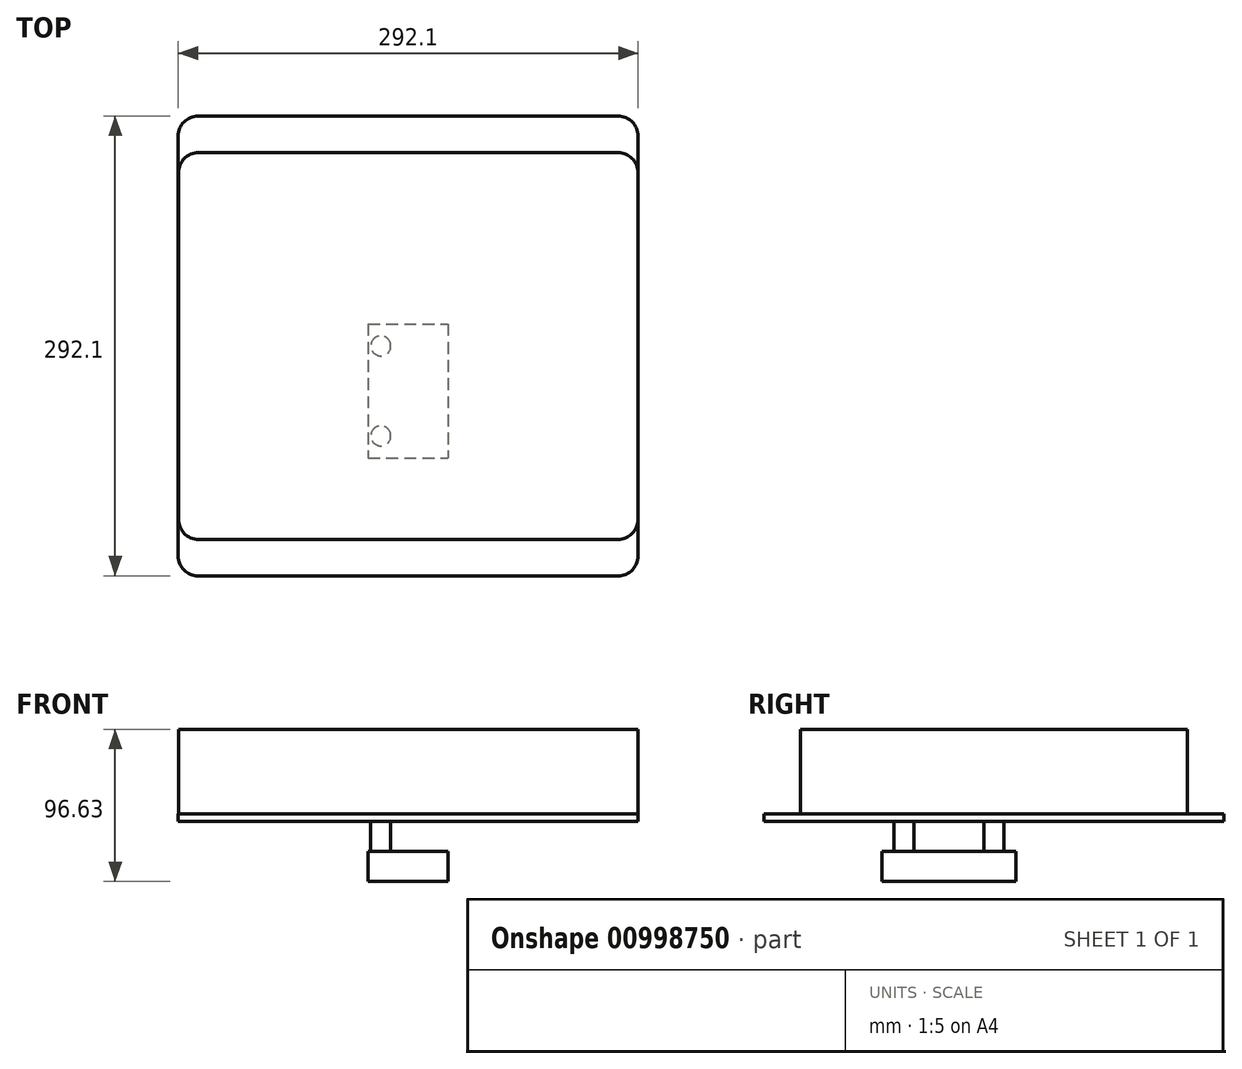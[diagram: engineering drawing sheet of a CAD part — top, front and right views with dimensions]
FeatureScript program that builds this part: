
annotation { "Feature Type Name" : "Feature", "Feature Type Description" : "" }
export const myFeature = defineFeature(function(context is Context, id is Id, definition is map)
    precondition{}
    {
        {
            var Q0;
            Q0=qCreatedBy(makeId("Top.planeOp"),FACE);
            var sketch = newSketch(context, id + "F0", { "sketchPlane" : qUnion([Q0])});
            skLineSegment(sketch, "E0.bottom", {"start": v(133.35, 146.05) * mm, "end": v(-133.35, 146.05) * mm});
            skLineSegment(sketch, "E0.top", {"start": v(133.35, -146.05) * mm, "end": v(-133.35, -146.05) * mm});
            skLineSegment(sketch, "E0.left", {"start": v(146.05, 133.35) * mm, "end": v(146.05, -133.35) * mm});
            skLineSegment(sketch, "E0.right", {"start": v(-146.05, 133.35) * mm, "end": v(-146.05, -133.35) * mm});
            skPoint(sketch, "E0.middle", {"position": v(0, 0) * mm});
            skPoint(sketch, "E1.visualSharp", {"position": v(-146.05, 146.05) * mm});
            skArc(sketch, "E1.filletArc", {"start": v(-133.35, 146.05) * mm, "mid": v(-142.33, 142.33) * mm, "end": v(-146.05, 133.35) * mm});
            skPoint(sketch, "E2.visualSharp", {"position": v(146.05, 146.05) * mm});
            skArc(sketch, "E2.filletArc", {"start": v(146.05, 133.35) * mm, "mid": v(142.33, 142.33) * mm, "end": v(133.35, 146.05) * mm});
            skPoint(sketch, "E3.visualSharp", {"position": v(146.05, -146.05) * mm});
            skArc(sketch, "E3.filletArc", {"start": v(133.35, -146.05) * mm, "mid": v(142.33, -142.33) * mm, "end": v(146.05, -133.35) * mm});
            skPoint(sketch, "E4.visualSharp", {"position": v(-146.05, -146.05) * mm});
            skArc(sketch, "E4.filletArc", {"start": v(-146.05, -133.35) * mm, "mid": v(-142.33, -142.33) * mm, "end": v(-133.35, -146.05) * mm});
            skSolve(sketch);
        }
        {
            var Q0;
            Q0=makeQuery(id+"F0.imprint","IMPRINT",FACE,{"disambiguationData":[TD([[makeQuery(id+"F0.imprint","IMPRINT",EDGE,{"derivedFrom":sQuery(id+"F0.wireOp",EDGE,"E0.bottom")}),1.0]])]});
            extrude(context, id + "F1", {"entities" : qUnion([Q0]), "depth" : 4.83 * mm, "offsetDistance" : 25.4 * mm});
        }
        {
            var Q0;
            Q0=qCreatedBy(makeId("Top.planeOp"),FACE);
            var sketch = newSketch(context, id + "F2", { "sketchPlane" : qUnion([Q0])});
            skCircle(sketch, "E5", {"center": v(-17.4, 0) * mm, "radius": 6.35 * mm});
            skCircle(sketch, "E6", {"center": v(-17.4, -57.15) * mm, "radius": 6.35 * mm});
            skCircle(sketch, "E7.MirrorC", {"center": v(17.4, 0) * mm, "radius": 6.35 * mm});
            skCircle(sketch, "E8.MirrorC", {"center": v(17.4, -57.15) * mm, "radius": 6.35 * mm});
            skSolve(sketch);
        }
        {
            var Q0;
            Q0=makeQuery(id+"F2.imprint","IMPRINT",FACE,{"disambiguationData":[TD([[makeQuery(id+"F2.imprint","IMPRINT",EDGE,{"derivedFrom":sQuery(id+"F2.wireOp",EDGE,"E6")}),1.0]])]});
            var Q1;
            Q1=makeQuery(id+"F2.imprint","IMPRINT",FACE,{"disambiguationData":[TD([[makeQuery(id+"F2.imprint","IMPRINT",EDGE,{"derivedFrom":sQuery(id+"F2.wireOp",EDGE,"E8.MirrorC")}),-1.0]])]});
            var Q2;
            Q2=makeQuery(id+"F2.imprint","IMPRINT",FACE,{"disambiguationData":[TD([[makeQuery(id+"F2.imprint","IMPRINT",EDGE,{"derivedFrom":sQuery(id+"F2.wireOp",EDGE,"E7.MirrorC")}),-1.0]])]});
            var Q3;
            Q3=makeQuery(id+"F2.imprint","IMPRINT",FACE,{"disambiguationData":[TD([[makeQuery(id+"F2.imprint","IMPRINT",EDGE,{"derivedFrom":sQuery(id+"F2.wireOp",EDGE,"E5")}),1.0]])]});
            extrude(context, id + "F3", {"entities" : qUnion([Q0, Q1, Q2, Q3]), "operationType" : NewBodyOperationType.ADD, "oppositeDirection" : true, "depth" : 19.05 * mm, "offsetDistance" : 25.4 * mm});
        }
        {
            var Q0;
            Q0=qCreatedBy(makeId("Top.planeOp"),FACE);
            cPlane(context, id + "F4", {"entities" : qUnion([Q0]), "cplaneType" : CPlaneType.OFFSET, "offset" : 19.05 * mm, "oppositeDirection" : true, "width" : 152.4 * mm, "height" : 152.4 * mm});
        }
        {
            var Q0;
            Q0=qCreatedBy(id+"F4.planeOp",FACE);
            var sketch = newSketch(context, id + "F5", { "sketchPlane" : qUnion([Q0])});
            skLineSegment(sketch, "E9.MirrorCS", {"start": v(-25.4, -71.12) * mm, "end": v(25.4, -71.12) * mm});
            skLineSegment(sketch, "E10.MirrorCS", {"start": v(25.4, 13.97) * mm, "end": v(25.4, -71.12) * mm});
            skLineSegment(sketch, "E11.MirrorCS", {"start": v(-25.4, 13.97) * mm, "end": v(-25.4, -71.12) * mm});
            skLineSegment(sketch, "E12.MirrorCS", {"start": v(-25.4, 13.97) * mm, "end": v(25.4, 13.97) * mm});
            skSolve(sketch);
        }
        {
            var Q0;
            Q0=makeQuery(id+"F5.imprint","IMPRINT",FACE,{"disambiguationData":[TD([[makeQuery(id+"F5.imprint","IMPRINT",EDGE,{"derivedFrom":sQuery(id+"F5.wireOp",EDGE,"E9.MirrorCS")}),1.0]])]});
            extrude(context, id + "F6", {"entities" : qUnion([Q0]), "operationType" : NewBodyOperationType.ADD, "oppositeDirection" : true, "depth" : 19.05 * mm, "offsetDistance" : 25.4 * mm});
        }
        {
            var Q0;
            Q0=makeQuery(id+"F1.opExtrude","CAP_FACE",FACE,{"disambiguationData":[OSD([sQuery(id+"F0.wireOp",EDGE,"E0.bottom"),sQuery(id+"F0.wireOp",EDGE,"E0.top"),sQuery(id+"F0.wireOp",EDGE,"E0.left"),sQuery(id+"F0.wireOp",EDGE,"E0.right"),sQuery(id+"F0.wireOp",EDGE,"E1.filletArc"),sQuery(id+"F0.wireOp",EDGE,"E2.filletArc"),sQuery(id+"F0.wireOp",EDGE,"E3.filletArc"),sQuery(id+"F0.wireOp",EDGE,"E4.filletArc")])],"isStart":false});
            var sketch = newSketch(context, id + "F7", { "sketchPlane" : qUnion([Q0])});
            skLineSegment(sketch, "E13.bottom", {"start": v(133.2, -122.85) * mm, "end": v(-133.2, -122.85) * mm});
            skLineSegment(sketch, "E13.top", {"start": v(133.2, 122.85) * mm, "end": v(-133.2, 122.85) * mm});
            skLineSegment(sketch, "E13.left", {"start": v(145.9, -110.15) * mm, "end": v(145.9, 110.15) * mm});
            skLineSegment(sketch, "E13.right", {"start": v(-145.9, -110.15) * mm, "end": v(-145.9, 110.15) * mm});
            skPoint(sketch, "E13.middle", {"position": v(0, 0) * mm});
            skPoint(sketch, "E14.visualSharp", {"position": v(-145.9, 122.85) * mm});
            skArc(sketch, "E14.filletArc", {"start": v(-133.2, 122.85) * mm, "mid": v(-142.18, 119.13) * mm, "end": v(-145.9, 110.15) * mm});
            skPoint(sketch, "E15.visualSharp", {"position": v(145.9, 122.85) * mm});
            skArc(sketch, "E15.filletArc", {"start": v(145.9, 110.15) * mm, "mid": v(142.18, 119.13) * mm, "end": v(133.2, 122.85) * mm});
            skPoint(sketch, "E16.visualSharp", {"position": v(145.9, -122.85) * mm});
            skArc(sketch, "E16.filletArc", {"start": v(133.2, -122.85) * mm, "mid": v(142.18, -119.13) * mm, "end": v(145.9, -110.15) * mm});
            skPoint(sketch, "E17.visualSharp", {"position": v(-145.9, -122.85) * mm});
            skArc(sketch, "E17.filletArc", {"start": v(-145.9, -110.15) * mm, "mid": v(-142.18, -119.13) * mm, "end": v(-133.2, -122.85) * mm});
            skSolve(sketch);
        }
        {
            var Q0;
            Q0=makeQuery(id+"F7.imprint","IMPRINT",FACE,{"disambiguationData":[TD([[makeQuery(id+"F7.imprint","IMPRINT",EDGE,{"derivedFrom":sQuery(id+"F7.wireOp",EDGE,"E13.bottom")}),-1.0]])]});
            extrude(context, id + "F8", {"entities" : qUnion([Q0]), "operationType" : NewBodyOperationType.ADD, "depth" : 53.7 * mm, "offsetDistance" : 25.4 * mm});
        }
    });
